# Revit family: Haworth_LIM_Light_Mounted
name_source: partatom
category: Lighting Fixtures
revit_build: Autodesk Revit 2018 (Build: 20170223_1515(x64)
units: mm (PartAtom-declared; Revit-internal decimal feet)

## family parameters
Always vertical = Yes
Cut with Voids When Loaded = No
Light Source = Yes
OmniClass Number = 23.80.70.11.14
OmniClass Title = General Luminaries, Directional
Part Type = Normal
Room Calculation Point = No
Round Connector Dimension = Use Diameter
Shared = No
Work Plane-Based = No

## types (2) — shared parameters
Actual Height = 14"
Actual Width = 26 1/2"
Add on Distance = 3 1/2"
Assembly Code = D5020200
Color Filter = 16777215
Description = Haworth LIM Light Mounted
Dimming Lamp Color Temperature Shift = <None>
Emit from Line Length = 17"
LEED Data = http://www.haworth.com
Lamp Finish = Haworth _ Metal _ Brushed Aluminum
Light Source Symbol Size = 17"
Manufacturer = Haworth
Model = LLxx-0023
Revision Number = 6
Size = Verify Final Dim. w/ Haworth
Sustainability Info = www.haworth.com/en-us/About-Us/Sustainability/Pages/Vision.aspx
URL = http://www.haworth.com
URL - Product = https://www.haworth.com
Warranty = http://www.haworth.com
Wattage Comments = 3 and 9 Watts 120 Volts 60 Hertz

## per-type parameters (varying)
| type | Light Source Height | Slat Mount | Under Mount |
| LLxx-0023 - Under Mount | 0" | No | Yes |
| LLxx-0023 - Slat Mount | 4 11/16" | Yes | No |

## geometry (parser evidence)
native form markers: Sweep x5
no freeform markers — native parametric forms only
